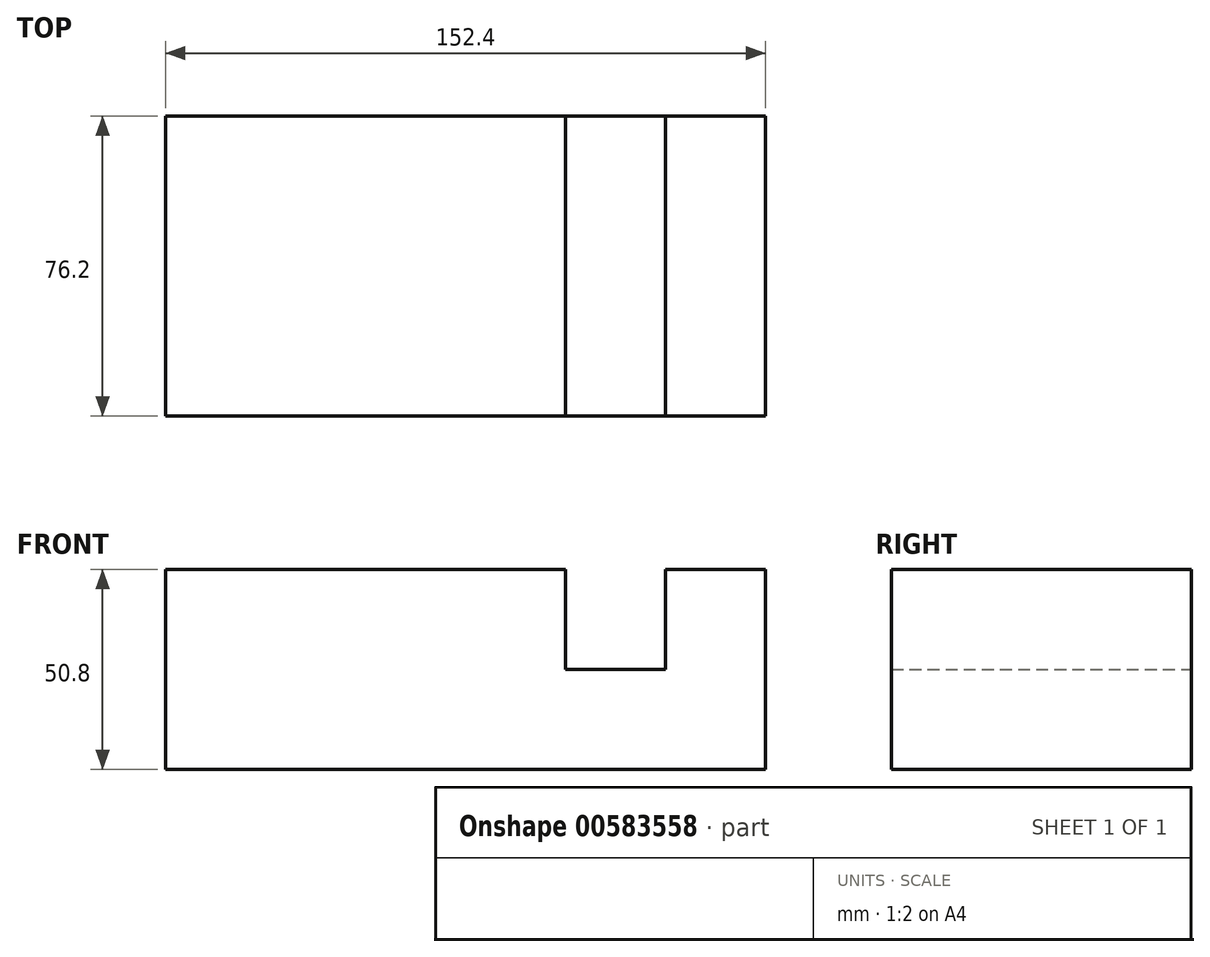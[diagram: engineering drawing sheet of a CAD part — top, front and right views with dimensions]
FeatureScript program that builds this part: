
annotation { "Feature Type Name" : "Feature", "Feature Type Description" : "" }
export const myFeature = defineFeature(function(context is Context, id is Id, definition is map)
    precondition{}
    {
        {
            var Q0;
            Q0=qCreatedBy(makeId("Front.planeOp"),FACE);
            var sketch = newSketch(context, id + "F0", { "sketchPlane" : qUnion([Q0])});
            skLineSegment(sketch, "E0", {"start": v(0, 0) * mm, "end": v(152.4, 0) * mm});
            skLineSegment(sketch, "E1", {"start": v(0, 0) * mm, "end": v(0, 50.8) * mm});
            skLineSegment(sketch, "E2", {"start": v(0, 50.8) * mm, "end": v(101.6, 50.8) * mm});
            skLineSegment(sketch, "E3", {"start": v(101.6, 50.8) * mm, "end": v(101.6, 25.4) * mm});
            skLineSegment(sketch, "E4", {"start": v(101.6, 25.4) * mm, "end": v(127, 25.4) * mm});
            skLineSegment(sketch, "E5", {"start": v(127, 25.4) * mm, "end": v(127, 50.8) * mm});
            skLineSegment(sketch, "E6", {"start": v(127, 50.8) * mm, "end": v(152.4, 50.8) * mm});
            skLineSegment(sketch, "E7", {"start": v(152.4, 50.8) * mm, "end": v(152.4, 0) * mm});
            skSolve(sketch);
        }
        {
            var Q0;
            Q0 = qSketchRegion(id + "F0", true);
            extrude(context, id + "F1", {"entities" : qUnion([Q0]), "depth" : 76.2 * mm, "offsetDistance" : 25.4 * mm});
        }
    });
